# Revit family: NAGARE_CURVED-INSIDE-45
name_source: partatom
category: Site
units: mm (PartAtom-declared; Revit-internal decimal feet)

## family parameters
Always vertical = Yes
Cut with Voids When Loaded = No
Part Type = Normal
Round Connector Dimension = Use Diameter
Shared = Yes
Work Plane-Based = Yes

## types (9) — shared parameters
Manufacturer = www.nagareconcrete.com
URL = https://www.nagareconcrete.com
materiaal_model = NAGARE_FME_(9-).f2_BETON_SI_BERSnl
offset_10 = 10 mm  [stored 0.0328084 ft]
voet_type2_hoogte = 850 mm
zero-valued in all types: Default Elevation

## per-type parameters (varying)
| type | Type Comments | beugelpositie_hoogte | model_hoogte | oksel_base-radial | oksel_maatvoering_breedte | oksel_maatvoering_hoogte | voet_hoogte | voet_lengte | zichtbaar_voet_type2 |
| C45LPI100/100 | C45LPI100/100 | 500 mm | 1000 mm | 1120 mm | 60 mm  [stored 0.19685 ft] | 60 mm  [stored 0.19685 ft] | 120 mm | 600 mm | No |
| C45LPI125/100 | C45LPI125/100 | 625 mm | 1250 mm | 1090 mm | 90 mm | 90 mm | 120 mm | 850 mm | No |
| C45LPI150/100 | C45LPI150/100 | 750 mm  [stored 2.46063 ft] | 1500 mm | 1090 mm | 90 mm | 90 mm | 120 mm | 850 mm | No |
| C45LPI175/100 | C45LPI175/100 | 750 mm  [stored 2.46063 ft] | 1750 mm | 1090 mm | 280 mm | 310 mm | 150 mm | 1100 mm | Yes |
| C45LPI200/100 | C45LPI200/100 | 750 mm  [stored 2.46063 ft] | 2000 mm | 1090 mm | 280 mm | 310 mm | 150 mm | 1100 mm | Yes |
| C45LPI225/100 | C45LPI225/100 | 750 mm  [stored 2.46063 ft] | 2250 mm | 1090 mm | 280 mm | 310 mm | 150 mm | 1100 mm | Yes |
| C45LPI250/100 | C45LPI250/100 | 750 mm  [stored 2.46063 ft] | 2500 mm | 1090 mm | 280 mm | 310 mm | 150 mm | 1100 mm | Yes |
| C45LPI50/100 | C45LPI150/100 | 750 mm  [stored 2.46063 ft] | 500 mm | 1090 mm | 60 mm  [stored 0.19685 ft] | 60 mm  [stored 0.19685 ft] | 120 mm | 600 mm | No |
| C45LPI75/100 | C45LPI75/100 | 375 mm  [stored 1.23031 ft] | 750 mm  [stored 2.46063 ft] | 1120 mm | 60 mm  [stored 0.19685 ft] | 60 mm  [stored 0.19685 ft] | 120 mm | 600 mm | No |

note: [stored X ft] marks values corroborated as IEEE doubles in the binary element streams (Revit-internal decimal feet)

## geometry (parser evidence)
native form markers: Sweep x2
no freeform markers — native parametric forms only
